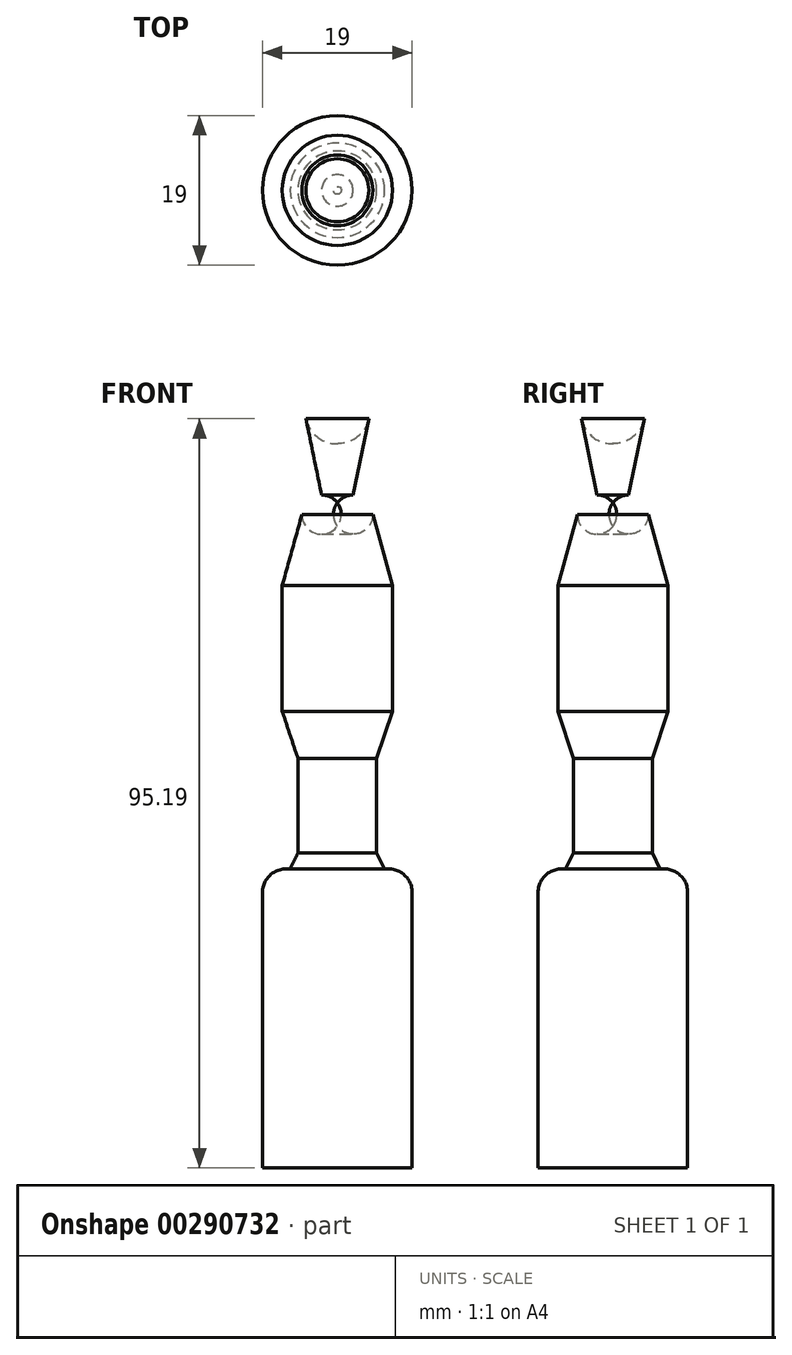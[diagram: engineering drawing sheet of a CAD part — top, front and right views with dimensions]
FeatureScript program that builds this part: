
annotation { "Feature Type Name" : "Feature", "Feature Type Description" : "" }
export const myFeature = defineFeature(function(context is Context, id is Id, definition is map)
    precondition{}
    {
        {
            var Q0;
            Q0=qCreatedBy(makeId("Front.planeOp"),FACE);
            var sketch = newSketch(context, id + "F0", { "sketchPlane" : qUnion([Q0])});
            skArc(sketch, "E0", {"start": v(4, -4.8) * mm, "mid": v(3.16, -1.44) * mm, "end": v(0, 0) * mm});
            skLineSegment(sketch, "E1", {"start": v(4, -4.8) * mm, "end": v(2, -14.5) * mm});
            skArc(sketch, "E2", {"start": v(4.5, -17) * mm, "mid": v(3.77, -15.23) * mm, "end": v(2, -14.5) * mm});
            skLineSegment(sketch, "E3", {"start": v(4.5, -17) * mm, "end": v(7, -26) * mm});
            skLineSegment(sketch, "E4", {"start": v(7, -26) * mm, "end": v(7, -42) * mm});
            skLineSegment(sketch, "E5", {"start": v(7, -42) * mm, "end": v(5, -48) * mm});
            skLineSegment(sketch, "E6", {"start": v(5, -48) * mm, "end": v(5, -60) * mm});
            skLineSegment(sketch, "E7", {"start": v(5, -60) * mm, "end": v(6, -62) * mm});
            skLineSegment(sketch, "E8", {"start": v(9.5, -65) * mm, "end": v(9.5, -100) * mm});
            skLineSegment(sketch, "E9", {"start": v(9.5, -100) * mm, "end": v(0, -100) * mm});
            skLineSegment(sketch, "E10", {"start": v(0, -100) * mm, "end": v(0, 0) * mm});
            skLineSegment(sketch, "E11", {"start": v(6, -62) * mm, "end": v(6.5, -62) * mm});
            skArc(sketch, "E12", {"start": v(9.5, -65) * mm, "mid": v(8.62, -62.88) * mm, "end": v(6.5, -62) * mm});
            skSolve(sketch);
        }
        {
            var Q0;
            Q0 = qSketchRegion(id + "F0", true);
            var Q1;
            Q1=sQuery(id+"F0.wireOp",EDGE,"E10");
            revolve(context, id + "F1", {"entities" : qUnion([Q0]), "axis" : qUnion([Q1]), "revolveType" : RevolveType.FULL});
        }
    });
